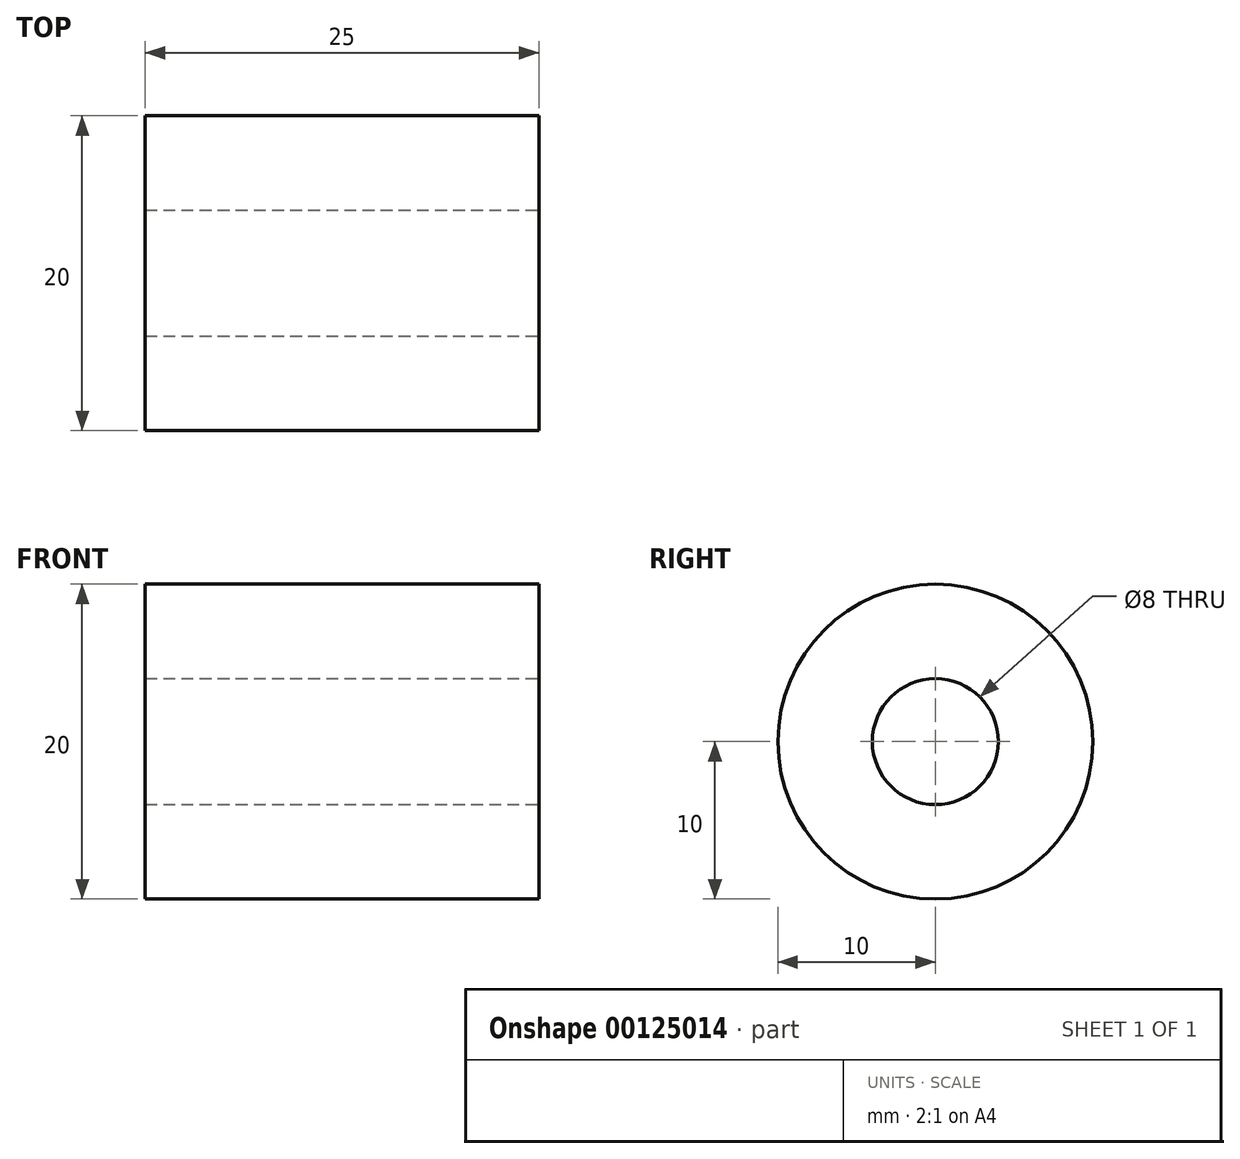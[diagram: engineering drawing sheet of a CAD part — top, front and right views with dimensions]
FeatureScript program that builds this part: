
annotation { "Feature Type Name" : "Feature", "Feature Type Description" : "" }
export const myFeature = defineFeature(function(context is Context, id is Id, definition is map)
    precondition{}
    {
        {
            var Q0;
            Q0=qCreatedBy(makeId("Right.planeOp"),FACE);
            var sketch = newSketch(context, id + "F0", { "sketchPlane" : qUnion([Q0])});
            skCircle(sketch, "E0", {"center": v(0, 0) * mm, "radius": 10 * mm});
            skSolve(sketch);
        }
        {
            var Q0;
            Q0 = qSketchRegion(id + "F0", true);
            extrude(context, id + "F1", {"entities" : qUnion([Q0]), "depth" : 25 * mm});
        }
        {
            var Q0;
            Q0=makeQuery(id+"F1.opExtrude","SWEPT_BODY",BODY,{"disambiguationData":[OSD([sQuery(id+"F0.wireOp",EDGE,"E0")])]});
            transform(context, id + "F2", {"entities" : qUnion([Q0]), "transformType" : TransformType.TRANSLATION_3D, "dx" : 0 * mm, "dy" : 0 * mm, "dz" : 0 * mm, "makeCopy" : true});
        }
        {
            var Q0;
            Q0=makeQuery(id+"F1.opExtrude","SWEPT_BODY",BODY,{"disambiguationData":[OSD([sQuery(id+"F0.wireOp",EDGE,"E0")])]});
            deleteBodies(context, id + "F3", {"entities" : qUnion([Q0])});
        }
        {
            var Q0;
            Q0=makeQuery(id+"F2.opPattern","COPY",FACE,{"derivedFrom":makeQuery(id+"F1.opExtrude","CAP_FACE",FACE,{"disambiguationData":[OSD([sQuery(id+"F0.wireOp",EDGE,"E0")])],"isStart":false}),"instanceName":"1"});
            var sketch = newSketch(context, id + "F4", { "sketchPlane" : qUnion([Q0])});
            skCircle(sketch, "E1", {"center": v(0, 0) * mm, "radius": 4 * mm});
            skSolve(sketch);
        }
        {
            var Q0;
            Q0 = qSketchRegion(id + "F4", true);
            extrude(context, id + "F5", {"entities" : qUnion([Q0]), "operationType" : NewBodyOperationType.REMOVE, "endBound" : BoundingType.UP_TO_NEXT, "oppositeDirection" : true, "depth" : 25 * mm});
        }
    });
